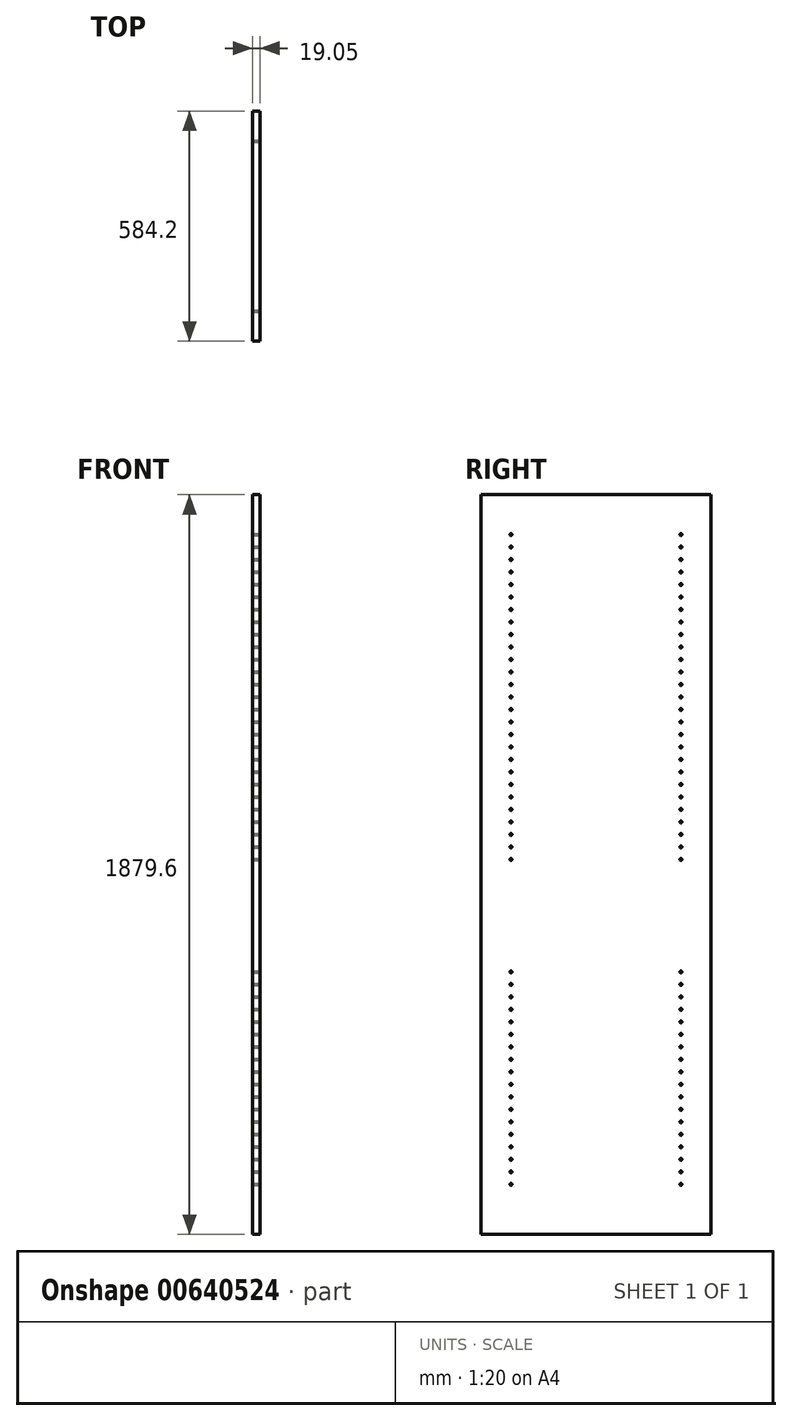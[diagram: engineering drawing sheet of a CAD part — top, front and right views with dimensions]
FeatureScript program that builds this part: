
annotation { "Feature Type Name" : "Feature", "Feature Type Description" : "" }
export const myFeature = defineFeature(function(context is Context, id is Id, definition is map)
    precondition{}
    {
        {
            var Q0;
            Q0=qCreatedBy(makeId("Right.planeOp"),FACE);
            var sketch = newSketch(context, id + "F0", { "sketchPlane" : qUnion([Q0])});
            skLineSegment(sketch, "E0.bottom", {"start": v(292.1, 939.8) * mm, "end": v(-292.1, 939.8) * mm});
            skLineSegment(sketch, "E0.top", {"start": v(292.1, -939.8) * mm, "end": v(-292.1, -939.8) * mm});
            skLineSegment(sketch, "E0.left", {"start": v(292.1, 939.8) * mm, "end": v(292.1, -939.8) * mm});
            skLineSegment(sketch, "E0.right", {"start": v(-292.1, 939.8) * mm, "end": v(-292.1, -939.8) * mm});
            skPoint(sketch, "E0.middle", {"position": v(0, 0) * mm});
            skSolve(sketch);
        }
        {
            var Q0;
            Q0=makeQuery(id+"F0.imprint","IMPRINT",FACE,{"disambiguationData":[TD([[makeQuery(id+"F0.imprint","IMPRINT",EDGE,{"derivedFrom":sQuery(id+"F0.wireOp",EDGE,"E0.bottom")}),1.0]])]});
            extrude(context, id + "F1", {"entities" : qUnion([Q0]), "depth" : 19.05 * mm, "offsetDistance" : 25.4 * mm});
        }
        {
            var Q0;
            Q0=makeQuery(id+"F1.opExtrude","CAP_FACE",FACE,{"disambiguationData":[OSD([sQuery(id+"F0.wireOp",EDGE,"E0.bottom"),sQuery(id+"F0.wireOp",EDGE,"E0.top"),sQuery(id+"F0.wireOp",EDGE,"E0.left"),sQuery(id+"F0.wireOp",EDGE,"E0.right")])],"isStart":false});
            var sketch = newSketch(context, id + "F2", { "sketchPlane" : qUnion([Q0])});
            skLineSegment(sketch, "E1", {"start": v(0, 939.8) * mm, "end": v(0, 806.45) * mm});
            skPoint(sketch, "E1.endSnap0", {"position": v(0, 939.8) * mm});
            skLineSegment(sketch, "E2.bottom", {"start": v(-215.9, 774.7) * mm, "end": v(215.9, 774.7) * mm});
            skLineSegment(sketch, "E2.top", {"start": v(-215.9, 838.2) * mm, "end": v(215.9, 838.2) * mm});
            skLineSegment(sketch, "E2.left", {"start": v(-215.9, 774.7) * mm, "end": v(-215.9, 838.2) * mm});
            skLineSegment(sketch, "E2.right", {"start": v(215.9, 774.7) * mm, "end": v(215.9, 838.2) * mm});
            skPoint(sketch, "E2.middle", {"position": v(0, 806.45) * mm});
            skLineSegment(sketch, "E3", {"start": v(0, 774.7) * mm, "end": v(0, 711.2) * mm});
            skPoint(sketch, "E3.endSnap0", {"position": v(0, 774.7) * mm});
            skLineSegment(sketch, "E4.bottom", {"start": v(-215.9, 742.95) * mm, "end": v(215.9, 742.95) * mm});
            skLineSegment(sketch, "E4.top", {"start": v(-215.9, 679.45) * mm, "end": v(215.9, 679.45) * mm});
            skLineSegment(sketch, "E4.left", {"start": v(-215.9, 742.95) * mm, "end": v(-215.9, 679.45) * mm});
            skLineSegment(sketch, "E4.right", {"start": v(215.9, 742.95) * mm, "end": v(215.9, 679.45) * mm});
            skPoint(sketch, "E4.middle", {"position": v(0, 711.2) * mm});
            skLineSegment(sketch, "E5", {"start": v(0, 679.45) * mm, "end": v(0, 615.95) * mm});
            skPoint(sketch, "E5.endSnap0", {"position": v(0, 679.45) * mm});
            skLineSegment(sketch, "E6.bottom", {"start": v(-215.9, 647.7) * mm, "end": v(215.9, 647.7) * mm});
            skLineSegment(sketch, "E6.top", {"start": v(-215.9, 584.2) * mm, "end": v(215.9, 584.2) * mm});
            skLineSegment(sketch, "E6.left", {"start": v(-215.9, 647.7) * mm, "end": v(-215.9, 584.2) * mm});
            skLineSegment(sketch, "E6.right", {"start": v(215.9, 647.7) * mm, "end": v(215.9, 584.2) * mm});
            skPoint(sketch, "E6.middle", {"position": v(0, 615.95) * mm});
            skPoint(sketch, "E6.cornerSnap0", {"position": v(-215.9, 711.2) * mm});
            skLineSegment(sketch, "E7", {"start": v(0, 584.2) * mm, "end": v(0, 520.7) * mm});
            skPoint(sketch, "E7.endSnap0", {"position": v(0, 584.2) * mm});
            skLineSegment(sketch, "E8.bottom", {"start": v(-215.9, 552.45) * mm, "end": v(215.9, 552.45) * mm});
            skLineSegment(sketch, "E8.top", {"start": v(-215.9, 488.95) * mm, "end": v(215.9, 488.95) * mm});
            skLineSegment(sketch, "E8.left", {"start": v(-215.9, 552.45) * mm, "end": v(-215.9, 488.95) * mm});
            skLineSegment(sketch, "E8.right", {"start": v(215.9, 552.45) * mm, "end": v(215.9, 488.95) * mm});
            skPoint(sketch, "E8.middle", {"position": v(0, 520.7) * mm});
            skLineSegment(sketch, "E9", {"start": v(0, 488.95) * mm, "end": v(0, 425.45) * mm});
            skLineSegment(sketch, "E10.bottom", {"start": v(-215.9, 457.2) * mm, "end": v(215.9, 457.2) * mm});
            skLineSegment(sketch, "E10.top", {"start": v(-215.9, 393.7) * mm, "end": v(215.9, 393.7) * mm});
            skLineSegment(sketch, "E10.left", {"start": v(-215.9, 457.2) * mm, "end": v(-215.9, 393.7) * mm});
            skLineSegment(sketch, "E10.right", {"start": v(215.9, 457.2) * mm, "end": v(215.9, 393.7) * mm});
            skPoint(sketch, "E10.middle", {"position": v(0, 425.45) * mm});
            skLineSegment(sketch, "E11", {"start": v(0, 393.7) * mm, "end": v(0, 330.2) * mm});
            skLineSegment(sketch, "E12.bottom", {"start": v(-215.9, 361.95) * mm, "end": v(215.9, 361.95) * mm});
            skLineSegment(sketch, "E12.top", {"start": v(-215.9, 298.45) * mm, "end": v(215.9, 298.45) * mm});
            skLineSegment(sketch, "E12.left", {"start": v(-215.9, 361.95) * mm, "end": v(-215.9, 298.45) * mm});
            skLineSegment(sketch, "E12.right", {"start": v(215.9, 361.95) * mm, "end": v(215.9, 298.45) * mm});
            skPoint(sketch, "E12.middle", {"position": v(0, 330.2) * mm});
            skPoint(sketch, "E12.cornerSnap0", {"position": v(0, 361.95) * mm});
            skLineSegment(sketch, "E13", {"start": v(0, 298.45) * mm, "end": v(0, 234.95) * mm});
            skLineSegment(sketch, "E14.bottom", {"start": v(-215.9, 266.7) * mm, "end": v(215.9, 266.7) * mm});
            skLineSegment(sketch, "E14.top", {"start": v(-215.9, 203.2) * mm, "end": v(215.9, 203.2) * mm});
            skLineSegment(sketch, "E14.left", {"start": v(-215.9, 266.7) * mm, "end": v(-215.9, 203.2) * mm});
            skLineSegment(sketch, "E14.right", {"start": v(215.9, 266.7) * mm, "end": v(215.9, 203.2) * mm});
            skPoint(sketch, "E14.middle", {"position": v(0, 234.95) * mm});
            skPoint(sketch, "E14.cornerSnap0", {"position": v(0, 266.7) * mm});
            skLineSegment(sketch, "E15", {"start": v(0, 203.2) * mm, "end": v(0, 139.7) * mm});
            skLineSegment(sketch, "E16.bottom", {"start": v(-215.9, 171.45) * mm, "end": v(215.9, 171.45) * mm});
            skLineSegment(sketch, "E16.top", {"start": v(-215.9, 107.95) * mm, "end": v(215.9, 107.95) * mm});
            skLineSegment(sketch, "E16.left", {"start": v(-215.9, 171.45) * mm, "end": v(-215.9, 107.95) * mm});
            skLineSegment(sketch, "E16.right", {"start": v(215.9, 171.45) * mm, "end": v(215.9, 107.95) * mm});
            skPoint(sketch, "E16.middle", {"position": v(0, 139.7) * mm});
            skPoint(sketch, "E16.cornerSnap0", {"position": v(0, 171.45) * mm});
            skLineSegment(sketch, "E17", {"start": v(0, 107.95) * mm, "end": v(0, 44.45) * mm});
            skPoint(sketch, "E17.endSnap0", {"position": v(0, 107.95) * mm});
            skLineSegment(sketch, "E18.bottom", {"start": v(-215.9, 76.2) * mm, "end": v(215.9, 76.2) * mm});
            skLineSegment(sketch, "E18.top", {"start": v(-215.9, 12.7) * mm, "end": v(215.9, 12.7) * mm});
            skLineSegment(sketch, "E18.left", {"start": v(-215.9, 76.2) * mm, "end": v(-215.9, 12.7) * mm});
            skLineSegment(sketch, "E18.right", {"start": v(215.9, 76.2) * mm, "end": v(215.9, 12.7) * mm});
            skPoint(sketch, "E18.middle", {"position": v(0, 44.45) * mm});
            skPoint(sketch, "E18.cornerSnap0", {"position": v(0, 76.2) * mm});
            skPoint(sketch, "E19.endSnap0", {"position": v(0, 12.7) * mm});
            skLineSegment(sketch, "E20", {"start": v(0, -241.3) * mm, "end": v(0, -304.8) * mm});
            skPoint(sketch, "E20.endSnap0", {"position": v(0, -146.05) * mm});
            skLineSegment(sketch, "E21.bottom", {"start": v(-215.9, -273.05) * mm, "end": v(215.9, -273.05) * mm});
            skLineSegment(sketch, "E21.top", {"start": v(-215.9, -336.55) * mm, "end": v(215.9, -336.55) * mm});
            skLineSegment(sketch, "E21.left", {"start": v(-215.9, -273.05) * mm, "end": v(-215.9, -336.55) * mm});
            skLineSegment(sketch, "E21.right", {"start": v(215.9, -273.05) * mm, "end": v(215.9, -336.55) * mm});
            skPoint(sketch, "E21.middle", {"position": v(0, -304.8) * mm});
            skPoint(sketch, "E21.cornerSnap0", {"position": v(0, -273.05) * mm});
            skLineSegment(sketch, "E22", {"start": v(0, -336.55) * mm, "end": v(0, -400.05) * mm});
            skPoint(sketch, "E22.endSnap0", {"position": v(0, -336.55) * mm});
            skLineSegment(sketch, "E23.bottom", {"start": v(-215.9, -368.3) * mm, "end": v(215.9, -368.3) * mm});
            skLineSegment(sketch, "E23.top", {"start": v(-215.9, -431.8) * mm, "end": v(215.9, -431.8) * mm});
            skLineSegment(sketch, "E23.left", {"start": v(-215.9, -368.3) * mm, "end": v(-215.9, -431.8) * mm});
            skLineSegment(sketch, "E23.right", {"start": v(215.9, -368.3) * mm, "end": v(215.9, -431.8) * mm});
            skPoint(sketch, "E23.middle", {"position": v(0, -400.05) * mm});
            skPoint(sketch, "E23.cornerSnap0", {"position": v(0, -368.3) * mm});
            skLineSegment(sketch, "E24", {"start": v(0, -431.8) * mm, "end": v(0, -495.3) * mm});
            skPoint(sketch, "E24.endSnap0", {"position": v(0, -431.8) * mm});
            skLineSegment(sketch, "E25.bottom", {"start": v(-215.9, -463.55) * mm, "end": v(215.9, -463.55) * mm});
            skLineSegment(sketch, "E25.top", {"start": v(-215.9, -527.05) * mm, "end": v(215.9, -527.05) * mm});
            skLineSegment(sketch, "E25.left", {"start": v(-215.9, -463.55) * mm, "end": v(-215.9, -527.05) * mm});
            skLineSegment(sketch, "E25.right", {"start": v(215.9, -463.55) * mm, "end": v(215.9, -527.05) * mm});
            skPoint(sketch, "E25.middle", {"position": v(0, -495.3) * mm});
            skPoint(sketch, "E25.cornerSnap0", {"position": v(0, -463.55) * mm});
            skLineSegment(sketch, "E26", {"start": v(0, -527.05) * mm, "end": v(0, -590.55) * mm});
            skPoint(sketch, "E26.endSnap0", {"position": v(0, -527.05) * mm});
            skLineSegment(sketch, "E27.bottom", {"start": v(-215.9, -558.8) * mm, "end": v(215.9, -558.8) * mm});
            skLineSegment(sketch, "E27.top", {"start": v(-215.9, -622.3) * mm, "end": v(215.9, -622.3) * mm});
            skLineSegment(sketch, "E27.left", {"start": v(-215.9, -558.8) * mm, "end": v(-215.9, -622.3) * mm});
            skLineSegment(sketch, "E27.right", {"start": v(215.9, -558.8) * mm, "end": v(215.9, -622.3) * mm});
            skPoint(sketch, "E27.middle", {"position": v(0, -590.55) * mm});
            skPoint(sketch, "E27.cornerSnap0", {"position": v(0, -558.8) * mm});
            skLineSegment(sketch, "E28", {"start": v(0, -622.3) * mm, "end": v(0, -685.8) * mm});
            skPoint(sketch, "E28.endSnap0", {"position": v(0, -622.3) * mm});
            skLineSegment(sketch, "E29.bottom", {"start": v(-215.9, -654.05) * mm, "end": v(215.9, -654.05) * mm});
            skLineSegment(sketch, "E29.top", {"start": v(-215.9, -717.55) * mm, "end": v(215.9, -717.55) * mm});
            skLineSegment(sketch, "E29.left", {"start": v(-215.9, -654.05) * mm, "end": v(-215.9, -717.55) * mm});
            skLineSegment(sketch, "E29.right", {"start": v(215.9, -654.05) * mm, "end": v(215.9, -717.55) * mm});
            skPoint(sketch, "E29.middle", {"position": v(0, -685.8) * mm});
            skPoint(sketch, "E29.cornerSnap0", {"position": v(0, -654.05) * mm});
            skLineSegment(sketch, "E30", {"start": v(0, -717.55) * mm, "end": v(0, -781.05) * mm});
            skPoint(sketch, "E30.endSnap0", {"position": v(0, -717.55) * mm});
            skLineSegment(sketch, "E31.bottom", {"start": v(-215.9, -749.3) * mm, "end": v(215.9, -749.3) * mm});
            skLineSegment(sketch, "E31.top", {"start": v(-215.9, -812.8) * mm, "end": v(215.9, -812.8) * mm});
            skLineSegment(sketch, "E31.left", {"start": v(-215.9, -749.3) * mm, "end": v(-215.9, -812.8) * mm});
            skLineSegment(sketch, "E31.right", {"start": v(215.9, -749.3) * mm, "end": v(215.9, -812.8) * mm});
            skPoint(sketch, "E31.middle", {"position": v(0, -781.05) * mm});
            skPoint(sketch, "E31.cornerSnap0", {"position": v(0, -749.3) * mm});
            skPoint(sketch, "E32", {"position": v(215.9, -812.8) * mm});
            skPoint(sketch, "E33", {"position": v(-215.9, -812.8) * mm});
            skPoint(sketch, "E34", {"position": v(-215.9, -781.05) * mm});
            skPoint(sketch, "E35", {"position": v(215.9, -781.05) * mm});
            skPoint(sketch, "E36", {"position": v(215.9, -749.3) * mm});
            skPoint(sketch, "E37", {"position": v(-215.9, -749.3) * mm});
            skPoint(sketch, "E38", {"position": v(-215.9, -717.55) * mm});
            skPoint(sketch, "E39", {"position": v(-215.9, -685.8) * mm});
            skPoint(sketch, "E40", {"position": v(-215.9, -654.05) * mm});
            skPoint(sketch, "E41", {"position": v(215.9, -717.55) * mm});
            skPoint(sketch, "E42", {"position": v(215.9, -685.8) * mm});
            skPoint(sketch, "E43", {"position": v(215.9, -654.05) * mm});
            skPoint(sketch, "E44", {"position": v(215.9, -622.3) * mm});
            skPoint(sketch, "E45", {"position": v(215.9, -590.55) * mm});
            skPoint(sketch, "E46", {"position": v(215.9, -558.8) * mm});
            skPoint(sketch, "E47", {"position": v(-215.9, -558.8) * mm});
            skPoint(sketch, "E48", {"position": v(-215.9, -590.55) * mm});
            skPoint(sketch, "E49", {"position": v(-215.9, -622.3) * mm});
            skPoint(sketch, "E50", {"position": v(-215.9, -527.05) * mm});
            skPoint(sketch, "E51", {"position": v(-215.9, -495.3) * mm});
            skPoint(sketch, "E52", {"position": v(-215.9, -463.55) * mm});
            skPoint(sketch, "E53", {"position": v(215.9, -463.55) * mm});
            skPoint(sketch, "E54", {"position": v(215.9, -495.3) * mm});
            skPoint(sketch, "E55", {"position": v(215.9, -527.05) * mm});
            skPoint(sketch, "E56", {"position": v(215.9, -431.8) * mm});
            skPoint(sketch, "E57", {"position": v(215.9, -400.05) * mm});
            skPoint(sketch, "E58", {"position": v(215.9, -368.3) * mm});
            skPoint(sketch, "E59", {"position": v(-215.9, -368.3) * mm});
            skPoint(sketch, "E60", {"position": v(-215.9, -400.05) * mm});
            skPoint(sketch, "E61", {"position": v(-215.9, -431.8) * mm});
            skPoint(sketch, "E62", {"position": v(-215.9, -336.55) * mm});
            skPoint(sketch, "E63", {"position": v(-215.9, -304.8) * mm});
            skPoint(sketch, "E64", {"position": v(-215.9, -273.05) * mm});
            skPoint(sketch, "E65", {"position": v(215.9, -273.05) * mm});
            skPoint(sketch, "E66", {"position": v(215.9, -304.8) * mm});
            skPoint(sketch, "E67", {"position": v(215.9, -336.55) * mm});
            skPoint(sketch, "E68", {"position": v(-215.9, 44.45) * mm});
            skPoint(sketch, "E69", {"position": v(-215.9, 76.2) * mm});
            skPoint(sketch, "E70", {"position": v(-215.9, 12.7) * mm});
            skPoint(sketch, "E71", {"position": v(215.9, 76.2) * mm});
            skPoint(sketch, "E72", {"position": v(215.9, 44.45) * mm});
            skPoint(sketch, "E73", {"position": v(215.9, 12.7) * mm});
            skPoint(sketch, "E74", {"position": v(215.9, 107.95) * mm});
            skPoint(sketch, "E75", {"position": v(215.9, 139.7) * mm});
            skPoint(sketch, "E76", {"position": v(215.9, 171.45) * mm});
            skPoint(sketch, "E77", {"position": v(-215.9, 171.45) * mm});
            skPoint(sketch, "E78", {"position": v(-215.9, 139.7) * mm});
            skPoint(sketch, "E79", {"position": v(-215.9, 107.95) * mm});
            skPoint(sketch, "E80", {"position": v(-215.9, 203.2) * mm});
            skPoint(sketch, "E81", {"position": v(-215.9, 234.95) * mm});
            skPoint(sketch, "E82", {"position": v(-215.9, 266.7) * mm});
            skPoint(sketch, "E83", {"position": v(215.9, 266.7) * mm});
            skPoint(sketch, "E84", {"position": v(215.9, 234.95) * mm});
            skPoint(sketch, "E85", {"position": v(215.9, 203.2) * mm});
            skPoint(sketch, "E86", {"position": v(215.9, 361.95) * mm});
            skPoint(sketch, "E87", {"position": v(215.9, 330.2) * mm});
            skPoint(sketch, "E88", {"position": v(215.9, 298.45) * mm});
            skPoint(sketch, "E89", {"position": v(-215.9, 298.45) * mm});
            skPoint(sketch, "E90", {"position": v(-215.9, 330.2) * mm});
            skPoint(sketch, "E91", {"position": v(-215.9, 361.95) * mm});
            skPoint(sketch, "E92", {"position": v(-215.9, 838.2) * mm});
            skPoint(sketch, "E93", {"position": v(-215.9, 806.45) * mm});
            skPoint(sketch, "E94", {"position": v(-215.9, 774.7) * mm});
            skPoint(sketch, "E95", {"position": v(-215.9, 742.95) * mm});
            skPoint(sketch, "E96", {"position": v(-215.9, 679.45) * mm});
            skPoint(sketch, "E97", {"position": v(-215.9, 647.7) * mm});
            skPoint(sketch, "E98", {"position": v(-215.9, 615.95) * mm});
            skPoint(sketch, "E99", {"position": v(-215.9, 584.2) * mm});
            skPoint(sketch, "E100", {"position": v(-215.9, 552.45) * mm});
            skPoint(sketch, "E101", {"position": v(-215.9, 520.7) * mm});
            skPoint(sketch, "E102", {"position": v(-215.9, 488.95) * mm});
            skPoint(sketch, "E103", {"position": v(-215.9, 457.2) * mm});
            skPoint(sketch, "E104", {"position": v(-215.9, 425.45) * mm});
            skPoint(sketch, "E105", {"position": v(-215.9, 393.7) * mm});
            skPoint(sketch, "E106", {"position": v(215.9, 838.2) * mm});
            skPoint(sketch, "E107", {"position": v(215.9, 806.45) * mm});
            skPoint(sketch, "E108", {"position": v(215.9, 774.7) * mm});
            skPoint(sketch, "E109", {"position": v(215.9, 742.95) * mm});
            skPoint(sketch, "E110", {"position": v(215.9, 711.2) * mm});
            skPoint(sketch, "E111", {"position": v(215.9, 679.45) * mm});
            skPoint(sketch, "E112", {"position": v(215.9, 647.7) * mm});
            skPoint(sketch, "E113", {"position": v(215.9, 615.95) * mm});
            skPoint(sketch, "E114", {"position": v(215.9, 584.2) * mm});
            skPoint(sketch, "E115", {"position": v(215.9, 552.45) * mm});
            skPoint(sketch, "E116", {"position": v(215.9, 520.7) * mm});
            skPoint(sketch, "E117", {"position": v(215.9, 488.95) * mm});
            skPoint(sketch, "E118", {"position": v(215.9, 457.2) * mm});
            skPoint(sketch, "E119", {"position": v(215.9, 425.45) * mm});
            skPoint(sketch, "E120", {"position": v(215.9, 393.7) * mm});
            skLineSegment(sketch, "E121", {"start": v(292.1, -939.8) * mm, "end": v(292.1, -127) * mm});
            skLineSegment(sketch, "E122", {"start": v(292.1, -127) * mm, "end": v(-292.1, -127) * mm});
            skLineSegment(sketch, "E123.bottom", {"start": v(-292.1, -127) * mm, "end": v(292.1, -127) * mm});
            skLineSegment(sketch, "E123.top", {"start": v(-292.1, -146.05) * mm, "end": v(292.1, -146.05) * mm});
            skLineSegment(sketch, "E123.left", {"start": v(-292.1, -127) * mm, "end": v(-292.1, -146.05) * mm});
            skLineSegment(sketch, "E123.right", {"start": v(292.1, -127) * mm, "end": v(292.1, -146.05) * mm});
            skSolve(sketch);
        }
        {
            var Q0;
            Q0=sQuery(id+"F2.wireOp",VERTEX,"E92");
            var Q1;
            Q1=sQuery(id+"F2.wireOp",VERTEX,"E93");
            var Q2;
            Q2=sQuery(id+"F2.wireOp",VERTEX,"E94");
            var Q3;
            Q3=sQuery(id+"F2.wireOp",VERTEX,"E95");
            var Q4;
            Q4=sQuery(id+"F2.wireOp",VERTEX,"E6.cornerSnap0");
            var Q5;
            Q5=sQuery(id+"F2.wireOp",VERTEX,"E96");
            var Q6;
            Q6=sQuery(id+"F2.wireOp",VERTEX,"E97");
            var Q7;
            Q7=sQuery(id+"F2.wireOp",VERTEX,"E98");
            var Q8;
            Q8=sQuery(id+"F2.wireOp",VERTEX,"E99");
            var Q9;
            Q9=sQuery(id+"F2.wireOp",VERTEX,"E100");
            var Q10;
            Q10=sQuery(id+"F2.wireOp",VERTEX,"E101");
            var Q11;
            Q11=sQuery(id+"F2.wireOp",VERTEX,"E102");
            var Q12;
            Q12=sQuery(id+"F2.wireOp",VERTEX,"E103");
            var Q13;
            Q13=sQuery(id+"F2.wireOp",VERTEX,"E104");
            var Q14;
            Q14=sQuery(id+"F2.wireOp",VERTEX,"E105");
            var Q15;
            Q15=sQuery(id+"F2.wireOp",VERTEX,"E91");
            var Q16;
            Q16=sQuery(id+"F2.wireOp",VERTEX,"E90");
            var Q17;
            Q17=sQuery(id+"F2.wireOp",VERTEX,"E89");
            var Q18;
            Q18=sQuery(id+"F2.wireOp",VERTEX,"E82");
            var Q19;
            Q19=sQuery(id+"F2.wireOp",VERTEX,"E81");
            var Q20;
            Q20=sQuery(id+"F2.wireOp",VERTEX,"E80");
            var Q21;
            Q21=sQuery(id+"F2.wireOp",VERTEX,"E77");
            var Q22;
            Q22=sQuery(id+"F2.wireOp",VERTEX,"E78");
            var Q23;
            Q23=sQuery(id+"F2.wireOp",VERTEX,"E79");
            var Q24;
            Q24=sQuery(id+"F2.wireOp",VERTEX,"E69");
            var Q25;
            Q25=sQuery(id+"F2.wireOp",VERTEX,"E68");
            var Q26;
            Q26=sQuery(id+"F2.wireOp",VERTEX,"E70");
            var Q27;
            Q27=sQuery(id+"F2.wireOp",VERTEX,"E64");
            var Q28;
            Q28=sQuery(id+"F2.wireOp",VERTEX,"E63");
            var Q29;
            Q29=sQuery(id+"F2.wireOp",VERTEX,"E62");
            var Q30;
            Q30=sQuery(id+"F2.wireOp",VERTEX,"E59");
            var Q31;
            Q31=sQuery(id+"F2.wireOp",VERTEX,"E60");
            var Q32;
            Q32=sQuery(id+"F2.wireOp",VERTEX,"E61");
            var Q33;
            Q33=sQuery(id+"F2.wireOp",VERTEX,"E51");
            var Q34;
            Q34=sQuery(id+"F2.wireOp",VERTEX,"E52");
            var Q35;
            Q35=sQuery(id+"F2.wireOp",VERTEX,"E50");
            var Q36;
            Q36=sQuery(id+"F2.wireOp",VERTEX,"E47");
            var Q37;
            Q37=sQuery(id+"F2.wireOp",VERTEX,"E48");
            var Q38;
            Q38=sQuery(id+"F2.wireOp",VERTEX,"E49");
            var Q39;
            Q39=sQuery(id+"F2.wireOp",VERTEX,"E40");
            var Q40;
            Q40=sQuery(id+"F2.wireOp",VERTEX,"E39");
            var Q41;
            Q41=sQuery(id+"F2.wireOp",VERTEX,"E38");
            var Q42;
            Q42=sQuery(id+"F2.wireOp",VERTEX,"E37");
            var Q43;
            Q43=sQuery(id+"F2.wireOp",VERTEX,"E34");
            var Q44;
            Q44=sQuery(id+"F2.wireOp",VERTEX,"E33");
            var Q45;
            Q45=sQuery(id+"F2.wireOp",VERTEX,"E32");
            var Q46;
            Q46=sQuery(id+"F2.wireOp",VERTEX,"E35");
            var Q47;
            Q47=sQuery(id+"F2.wireOp",VERTEX,"E36");
            var Q48;
            Q48=sQuery(id+"F2.wireOp",VERTEX,"E41");
            var Q49;
            Q49=sQuery(id+"F2.wireOp",VERTEX,"E42");
            var Q50;
            Q50=sQuery(id+"F2.wireOp",VERTEX,"E43");
            var Q51;
            Q51=sQuery(id+"F2.wireOp",VERTEX,"E44");
            var Q52;
            Q52=sQuery(id+"F2.wireOp",VERTEX,"E45");
            var Q53;
            Q53=sQuery(id+"F2.wireOp",VERTEX,"E46");
            var Q54;
            Q54=sQuery(id+"F2.wireOp",VERTEX,"E55");
            var Q55;
            Q55=sQuery(id+"F2.wireOp",VERTEX,"E54");
            var Q56;
            Q56=sQuery(id+"F2.wireOp",VERTEX,"E53");
            var Q57;
            Q57=sQuery(id+"F2.wireOp",VERTEX,"E56");
            var Q58;
            Q58=sQuery(id+"F2.wireOp",VERTEX,"E57");
            var Q59;
            Q59=sQuery(id+"F2.wireOp",VERTEX,"E58");
            var Q60;
            Q60=sQuery(id+"F2.wireOp",VERTEX,"E67");
            var Q61;
            Q61=sQuery(id+"F2.wireOp",VERTEX,"E66");
            var Q62;
            Q62=sQuery(id+"F2.wireOp",VERTEX,"E65");
            var Q63;
            Q63=sQuery(id+"F2.wireOp",VERTEX,"E73");
            var Q64;
            Q64=sQuery(id+"F2.wireOp",VERTEX,"E72");
            var Q65;
            Q65=sQuery(id+"F2.wireOp",VERTEX,"E71");
            var Q66;
            Q66=sQuery(id+"F2.wireOp",VERTEX,"E74");
            var Q67;
            Q67=sQuery(id+"F2.wireOp",VERTEX,"E75");
            var Q68;
            Q68=sQuery(id+"F2.wireOp",VERTEX,"E76");
            var Q69;
            Q69=sQuery(id+"F2.wireOp",VERTEX,"E85");
            var Q70;
            Q70=sQuery(id+"F2.wireOp",VERTEX,"E83");
            var Q71;
            Q71=sQuery(id+"F2.wireOp",VERTEX,"E84");
            var Q72;
            Q72=sQuery(id+"F2.wireOp",VERTEX,"E88");
            var Q73;
            Q73=sQuery(id+"F2.wireOp",VERTEX,"E87");
            var Q74;
            Q74=sQuery(id+"F2.wireOp",VERTEX,"E86");
            var Q75;
            Q75=sQuery(id+"F2.wireOp",VERTEX,"E118");
            var Q76;
            Q76=sQuery(id+"F2.wireOp",VERTEX,"E119");
            var Q77;
            Q77=sQuery(id+"F2.wireOp",VERTEX,"E120");
            var Q78;
            Q78=sQuery(id+"F2.wireOp",VERTEX,"E117");
            var Q79;
            Q79=sQuery(id+"F2.wireOp",VERTEX,"E116");
            var Q80;
            Q80=sQuery(id+"F2.wireOp",VERTEX,"E115");
            var Q81;
            Q81=sQuery(id+"F2.wireOp",VERTEX,"E113");
            var Q82;
            Q82=sQuery(id+"F2.wireOp",VERTEX,"E114");
            var Q83;
            Q83=sQuery(id+"F2.wireOp",VERTEX,"E112");
            var Q84;
            Q84=sQuery(id+"F2.wireOp",VERTEX,"E111");
            var Q85;
            Q85=sQuery(id+"F2.wireOp",VERTEX,"E110");
            var Q86;
            Q86=sQuery(id+"F2.wireOp",VERTEX,"E109");
            var Q87;
            Q87=sQuery(id+"F2.wireOp",VERTEX,"E108");
            var Q88;
            Q88=sQuery(id+"F2.wireOp",VERTEX,"E107");
            var Q89;
            Q89=sQuery(id+"F2.wireOp",VERTEX,"E106");
            var Q90;
            Q90=makeQuery(id+"F1.opExtrude","SWEPT_BODY",BODY,{"disambiguationData":[OSD([sQuery(id+"F0.wireOp",EDGE,"E0.bottom"),sQuery(id+"F0.wireOp",EDGE,"E0.top"),sQuery(id+"F0.wireOp",EDGE,"E0.left"),sQuery(id+"F0.wireOp",EDGE,"E0.right")])]});
            hole(context, id + "F3", {"style" : HoleStyle.SIMPLE, "endStyle" : HoleEndStyle.BLIND, "holeDiameter" : 5 * mm, "majorDiameter" : 6.35 * mm, "holeDepth" : 14.22 * mm, "isTappedThrough" : true, "tappedDepth" : 12.7 * mm, "tapClearance" : 3, "startFromSketch" : true, "locations" : qUnion([Q0, Q1, Q2, Q3, Q4, Q5, Q6, Q7, Q8, Q9, Q10, Q11, Q12, Q13, Q14, Q15, Q16, Q17, Q18, Q19, Q20, Q21, Q22, Q23, Q24, Q25, Q26, Q27, Q28, Q29, Q30, Q31, Q32, Q33, Q34, Q35, Q36, Q37, Q38, Q39, Q40, Q41, Q42, Q43, Q44, Q45, Q46, Q47, Q48, Q49, Q50, Q51, Q52, Q53, Q54, Q55, Q56, Q57, Q58, Q59, Q60, Q61, Q62, Q63, Q64, Q65, Q66, Q67, Q68, Q69, Q70, Q71, Q72, Q73, Q74, Q75, Q76, Q77, Q78, Q79, Q80, Q81, Q82, Q83, Q84, Q85, Q86, Q87, Q88, Q89]), "scope" : qUnion([Q90])});
        }
    });
